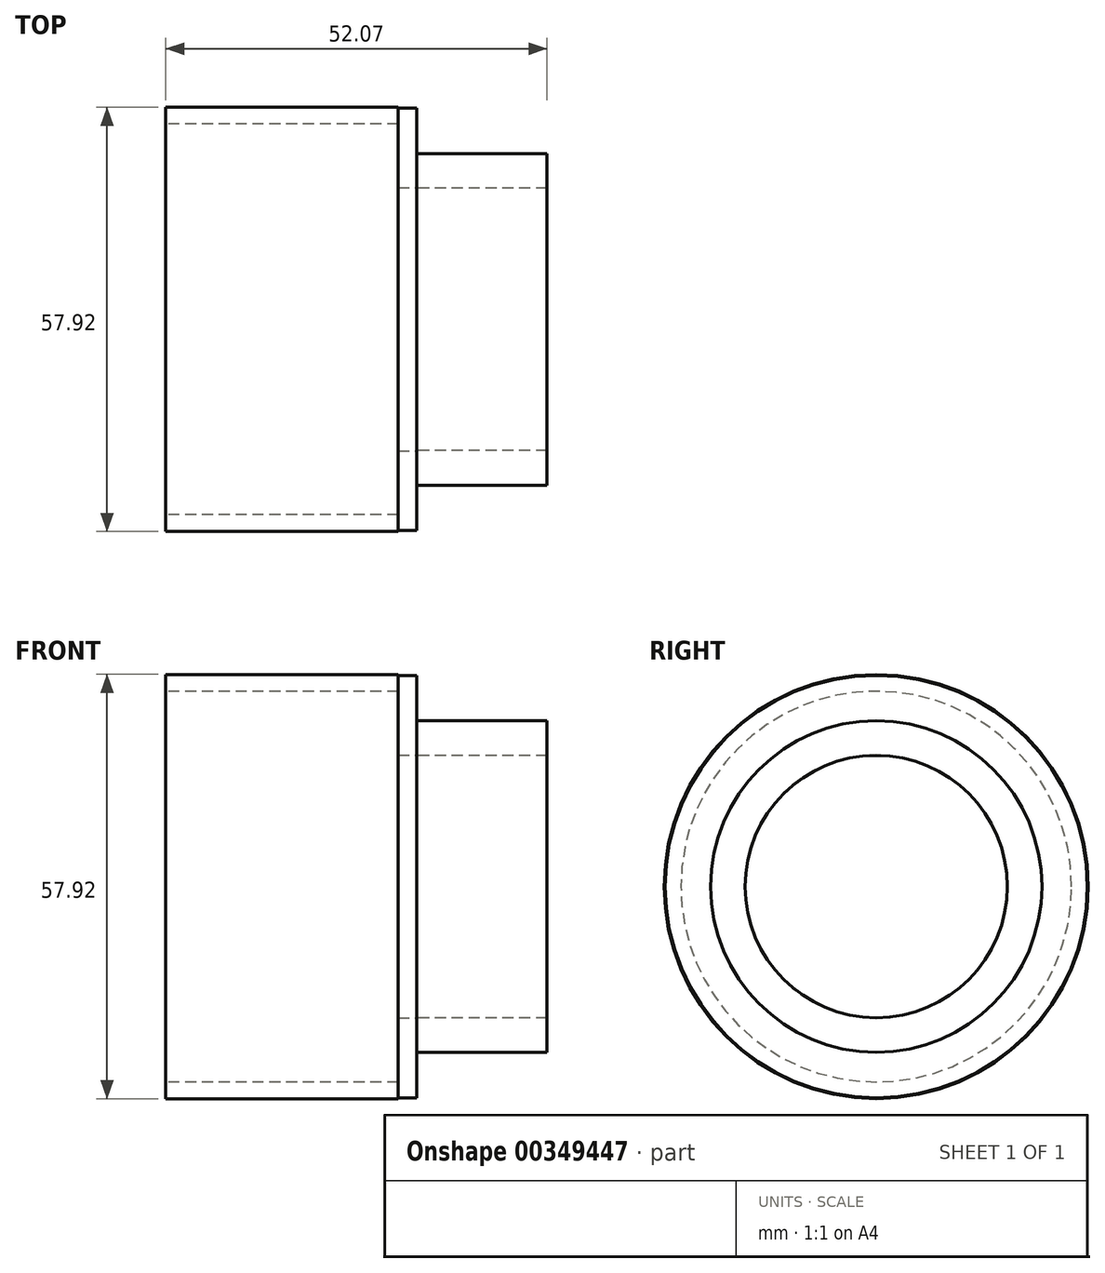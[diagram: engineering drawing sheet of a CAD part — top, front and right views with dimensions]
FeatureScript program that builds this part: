
annotation { "Feature Type Name" : "Feature", "Feature Type Description" : "" }
export const myFeature = defineFeature(function(context is Context, id is Id, definition is map)
    precondition{}
    {
        {
            var Q0;
            Q0=qCreatedBy(makeId("Right.planeOp"),FACE);
            var sketch = newSketch(context, id + "F0", { "sketchPlane" : qUnion([Q0])});
            skCircle(sketch, "E0", {"center": v(0, 0) * mm, "radius": 28.96 * mm});
            skCircle(sketch, "E1", {"center": v(0, 0) * mm, "radius": 26.67 * mm});
            skSolve(sketch);
        }
        {
            var Q0;
            Q0 = qSketchRegion(id + "F0", true);
            extrude(context, id + "F1", {"entities" : qUnion([Q0]), "depth" : 31.75 * mm});
        }
        {
            var Q0;
            Q0=makeQuery(id+"F1.opExtrude","CAP_FACE",FACE,{"disambiguationData":[OSD([sQuery(id+"F0.wireOp",EDGE,"E0"),sQuery(id+"F0.wireOp",EDGE,"E1")])],"isStart":false});
            var sketch = newSketch(context, id + "F2", { "sketchPlane" : qUnion([Q0])});
            skCircle(sketch, "E2", {"center": v(0, 0) * mm, "radius": 28.83 * mm});
            skSolve(sketch);
        }
        {
            var Q0;
            Q0 = qSketchRegion(id + "F2", true);
            extrude(context, id + "F3", {"entities" : qUnion([Q0]), "operationType" : NewBodyOperationType.ADD, "depth" : 2.54 * mm});
        }
        {
            var Q0;
            Q0=makeQuery(id+"F3.opExtrude","CAP_FACE",FACE,{"disambiguationData":[OSD([sQuery(id+"F2.wireOp",EDGE,"E2")])],"isStart":false});
            var sketch = newSketch(context, id + "F4", { "sketchPlane" : qUnion([Q0])});
            skCircle(sketch, "E3", {"center": v(0, 0) * mm, "radius": 17.9 * mm});
            skCircle(sketch, "E4", {"center": v(0, 0) * mm, "radius": 22.63 * mm});
            skSolve(sketch);
        }
        {
            var Q0;
            Q0 = qSketchRegion(id + "F4", true);
            extrude(context, id + "F5", {"entities" : qUnion([Q0]), "operationType" : NewBodyOperationType.ADD, "depth" : 17.78 * mm});
        }
        {
            var Q0;
            {var subQ0=sQuery(id+"F2.wireOp",EDGE,"E2");Q0=makeQuery(id+"F5.boolean.opBoolean","SPLIT",FACE,{"disambiguationData":[TD([makeQuery(id+"F3.opExtrude","SWEPT_FACE",FACE,{"disambiguationData":[OSD([subQ0])]})])],"derivedFrom":makeQuery(id+"F3.opExtrude","CAP_FACE",FACE,{"disambiguationData":[OSD([subQ0])],"isStart":false})});}
            var sketch = newSketch(context, id + "F6", { "sketchPlane" : qUnion([Q0])});
            skCircle(sketch, "E5", {"center": v(0, 0) * mm, "radius": 17.97 * mm});
            skSolve(sketch);
        }
        {
            var Q0;
            Q0 = qSketchRegion(id + "F6", true);
            var Q1;
            Q1=makeQuery(id+"F3.opExtrude","CAP_FACE",FACE,{"disambiguationData":[OSD([sQuery(id+"F2.wireOp",EDGE,"E2")])],"isStart":true});
            extrude(context, id + "F7", {"entities" : qUnion([Q0]), "operationType" : NewBodyOperationType.REMOVE, "endBound" : BoundingType.UP_TO_SURFACE, "oppositeDirection" : true, "endBoundEntityFace" : qUnion([Q1]), "depth" : -2.54 * mm});
        }
    });
